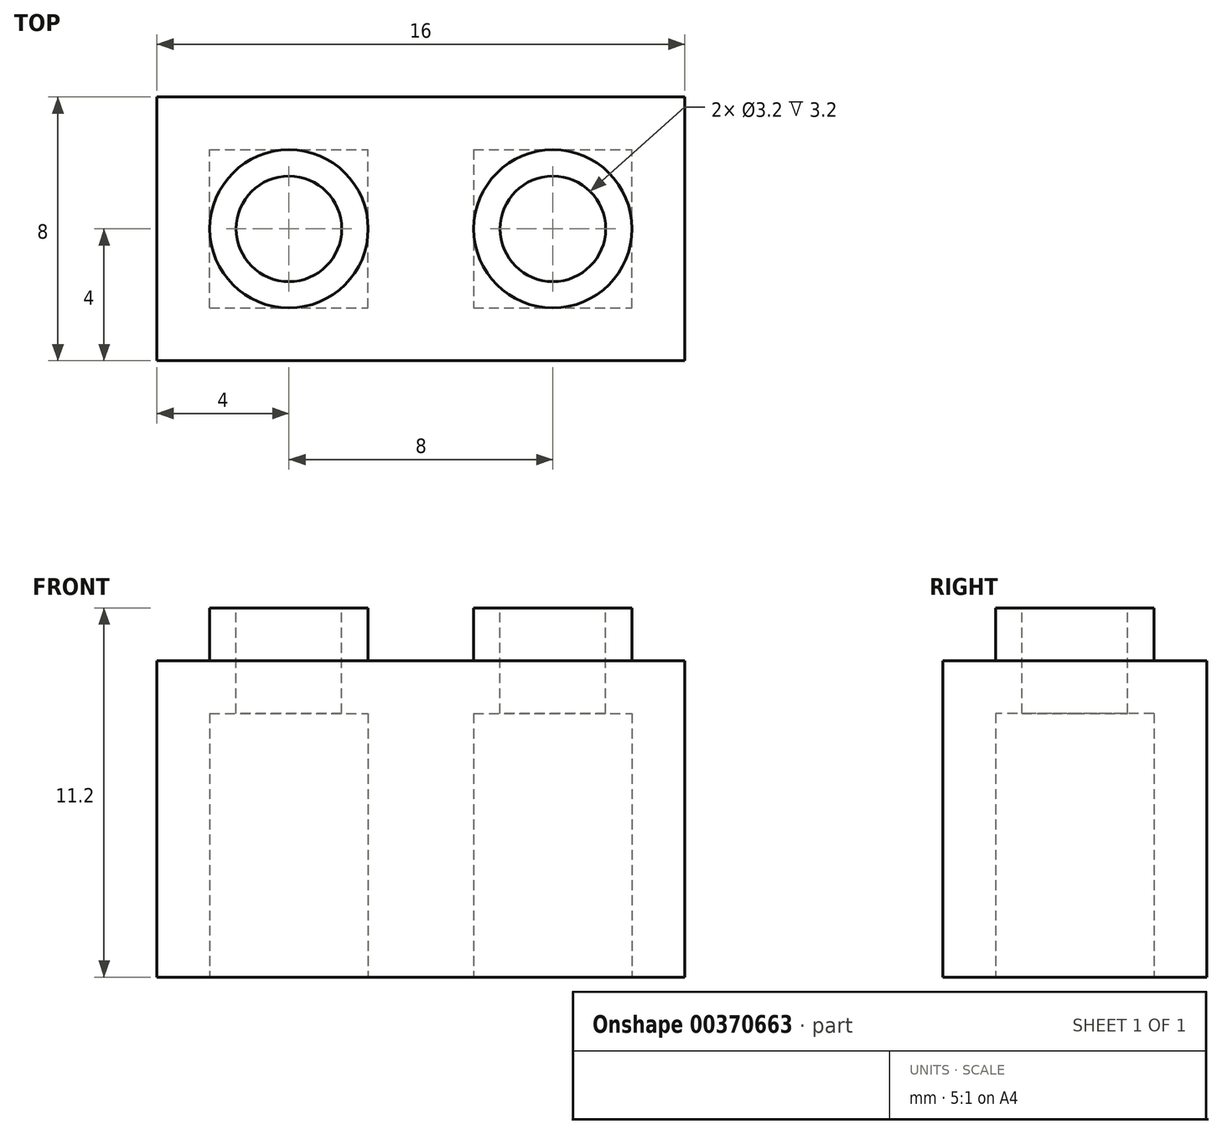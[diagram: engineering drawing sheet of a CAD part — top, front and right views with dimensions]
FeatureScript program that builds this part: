
annotation { "Feature Type Name" : "Feature", "Feature Type Description" : "" }
export const myFeature = defineFeature(function(context is Context, id is Id, definition is map)
    precondition{}
    {
        {
            var Q0;
            Q0=qCreatedBy(makeId("Top.planeOp"),FACE);
            var sketch = newSketch(context, id + "F0", { "sketchPlane" : qUnion([Q0])});
            skLineSegment(sketch, "E0.bottom", {"start": v(-8, -4) * mm, "end": v(8, -4) * mm});
            skLineSegment(sketch, "E0.top", {"start": v(-8, 4) * mm, "end": v(8, 4) * mm});
            skLineSegment(sketch, "E0.left", {"start": v(-8, -4) * mm, "end": v(-8, 4) * mm});
            skLineSegment(sketch, "E0.right", {"start": v(8, -4) * mm, "end": v(8, 4) * mm});
            skPoint(sketch, "E0.middle", {"position": v(0, 0) * mm});
            skLineSegment(sketch, "E1.0", {"start": v(-6.4, -2.4) * mm, "end": v(6.4, -2.4) * mm});
            skLineSegment(sketch, "E1.1", {"start": v(-6.4, -2.4) * mm, "end": v(-6.4, 2.4) * mm});
            skLineSegment(sketch, "E1.2", {"start": v(-6.4, 2.4) * mm, "end": v(6.4, 2.4) * mm});
            skLineSegment(sketch, "E1.3", {"start": v(6.4, -2.4) * mm, "end": v(6.4, 2.4) * mm});
            skLineSegment(sketch, "E2", {"start": v(-1.6, -2.4) * mm, "end": v(-1.6, 2.4) * mm});
            skLineSegment(sketch, "E3", {"start": v(1.6, -2.4) * mm, "end": v(1.6, 2.4) * mm});
            skSolve(sketch);
        }
        {
            var Q0;
            Q0=makeQuery(id+"F0.imprint","IMPRINT",FACE,{"disambiguationData":[TD([[makeQuery(id+"F0.imprint","IMPRINT",EDGE,{"derivedFrom":sQuery(id+"F0.wireOp",EDGE,"E0.bottom")}),1.0]])]});
            var Q1;
            Q1=makeQuery(id+"F0.imprint","IMPRINT",FACE,{"disambiguationData":[TD([[makeQuery(id+"F0.imprint","IMPRINT",EDGE,{"derivedFrom":sQuery(id+"F0.wireOp",EDGE,"E1.0")}),1.0]])]});
            extrude(context, id + "F1", {"entities" : qUnion([Q0, Q1]), "depth" : 9.6 * mm});
        }
        {
            var Q0;
            Q0=makeQuery(id+"F0.imprint","IMPRINT",FACE,{"disambiguationData":[TD([[makeQuery(id+"F0.imprint","IMPRINT",EDGE,{"derivedFrom":sQuery(id+"F0.wireOp",EDGE,"E1.0")}),1.0]])]});
            extrude(context, id + "F2", {"entities" : qUnion([Q0]), "operationType" : NewBodyOperationType.REMOVE, "depth" : 8 * mm});
        }
        {
            var Q0;
            {var subQ0=sQuery(id+"F0.wireOp",EDGE,"E2");Q0=makeQuery(id+"F0.imprint","IMPRINT",FACE,{"disambiguationData":[TD([[makeQuery(id+"F0.imprint","IMPRINT",EDGE,{"derivedFrom":subQ0}),-1.0]])]});}
            extrude(context, id + "F3", {"entities" : qUnion([Q0]), "operationType" : NewBodyOperationType.ADD, "depth" : 9.6 * mm});
        }
        {
            var Q0;
            Q0=makeQuery(id+"F1.opExtrude","CAP_FACE",FACE,{"disambiguationData":[OSD([sQuery(id+"F0.wireOp",EDGE,"E0.bottom"),sQuery(id+"F0.wireOp",EDGE,"E0.top"),sQuery(id+"F0.wireOp",EDGE,"E0.left"),sQuery(id+"F0.wireOp",EDGE,"E0.right")])],"isStart":false});
            var sketch = newSketch(context, id + "F4", { "sketchPlane" : qUnion([Q0])});
            skCircle(sketch, "E4", {"center": v(4, 0) * mm, "radius": 1.6 * mm});
            skCircle(sketch, "E5", {"center": v(-4, 0) * mm, "radius": 1.6 * mm});
            skSolve(sketch);
        }
        {
            var Q0;
            Q0=makeQuery(id+"F4.imprint","IMPRINT",FACE,{"disambiguationData":[TD([[makeQuery(id+"F4.imprint","IMPRINT",EDGE,{"derivedFrom":sQuery(id+"F4.wireOp",EDGE,"E5")}),1.0]])]});
            var Q1;
            Q1=makeQuery(id+"F4.imprint","IMPRINT",FACE,{"disambiguationData":[TD([[makeQuery(id+"F4.imprint","IMPRINT",EDGE,{"derivedFrom":sQuery(id+"F4.wireOp",EDGE,"E4")}),1.0]])]});
            extrude(context, id + "F5", {"entities" : qUnion([Q0, Q1]), "operationType" : NewBodyOperationType.REMOVE, "oppositeDirection" : true, "depth" : 1.6 * mm});
        }
        {
            var Q0;
            Q0=makeQuery(id+"F1.opExtrude","CAP_FACE",FACE,{"disambiguationData":[OSD([sQuery(id+"F0.wireOp",EDGE,"E0.bottom"),sQuery(id+"F0.wireOp",EDGE,"E0.top"),sQuery(id+"F0.wireOp",EDGE,"E0.left"),sQuery(id+"F0.wireOp",EDGE,"E0.right")])],"isStart":false});
            var sketch = newSketch(context, id + "F6", { "sketchPlane" : qUnion([Q0])});
            skCircle(sketch, "E6", {"center": v(4, 0) * mm, "radius": 2.4 * mm});
            skCircle(sketch, "E7", {"center": v(-4, 0) * mm, "radius": 2.4 * mm});
            skSolve(sketch);
        }
        {
            var Q0;
            Q0=makeQuery(id+"F6.imprint","IMPRINT",FACE,{"disambiguationData":[TD([[makeQuery(id+"F6.imprint","IMPRINT",EDGE,{"derivedFrom":sQuery(id+"F6.wireOp",EDGE,"E7")}),1.0]])]});
            var Q1;
            Q1=makeQuery(id+"F6.imprint","IMPRINT",FACE,{"disambiguationData":[TD([[makeQuery(id+"F6.imprint","IMPRINT",EDGE,{"derivedFrom":makeQuery(id+"F5.boolean.opBoolean","COPY",EDGE,{"derivedFrom":makeQuery(id+"F5.opExtrude","CAP_EDGE",EDGE,{"disambiguationData":[OSD([sQuery(id+"F4.wireOp",EDGE,"E5")])],"isStart":true})})}),1.0]])]});
            var Q2;
            Q2=makeQuery(id+"F6.imprint","IMPRINT",FACE,{"disambiguationData":[TD([[makeQuery(id+"F6.imprint","IMPRINT",EDGE,{"derivedFrom":makeQuery(id+"F5.boolean.opBoolean","COPY",EDGE,{"derivedFrom":makeQuery(id+"F5.opExtrude","CAP_EDGE",EDGE,{"disambiguationData":[OSD([sQuery(id+"F4.wireOp",EDGE,"E4")])],"isStart":true})})}),1.0]])]});
            var Q3;
            Q3=makeQuery(id+"F6.imprint","IMPRINT",FACE,{"disambiguationData":[TD([[makeQuery(id+"F6.imprint","IMPRINT",EDGE,{"derivedFrom":sQuery(id+"F6.wireOp",EDGE,"E6")}),1.0]])]});
            extrude(context, id + "F7", {"entities" : qUnion([Q0, Q1, Q2, Q3]), "operationType" : NewBodyOperationType.ADD, "depth" : 1.6 * mm});
        }
    });
